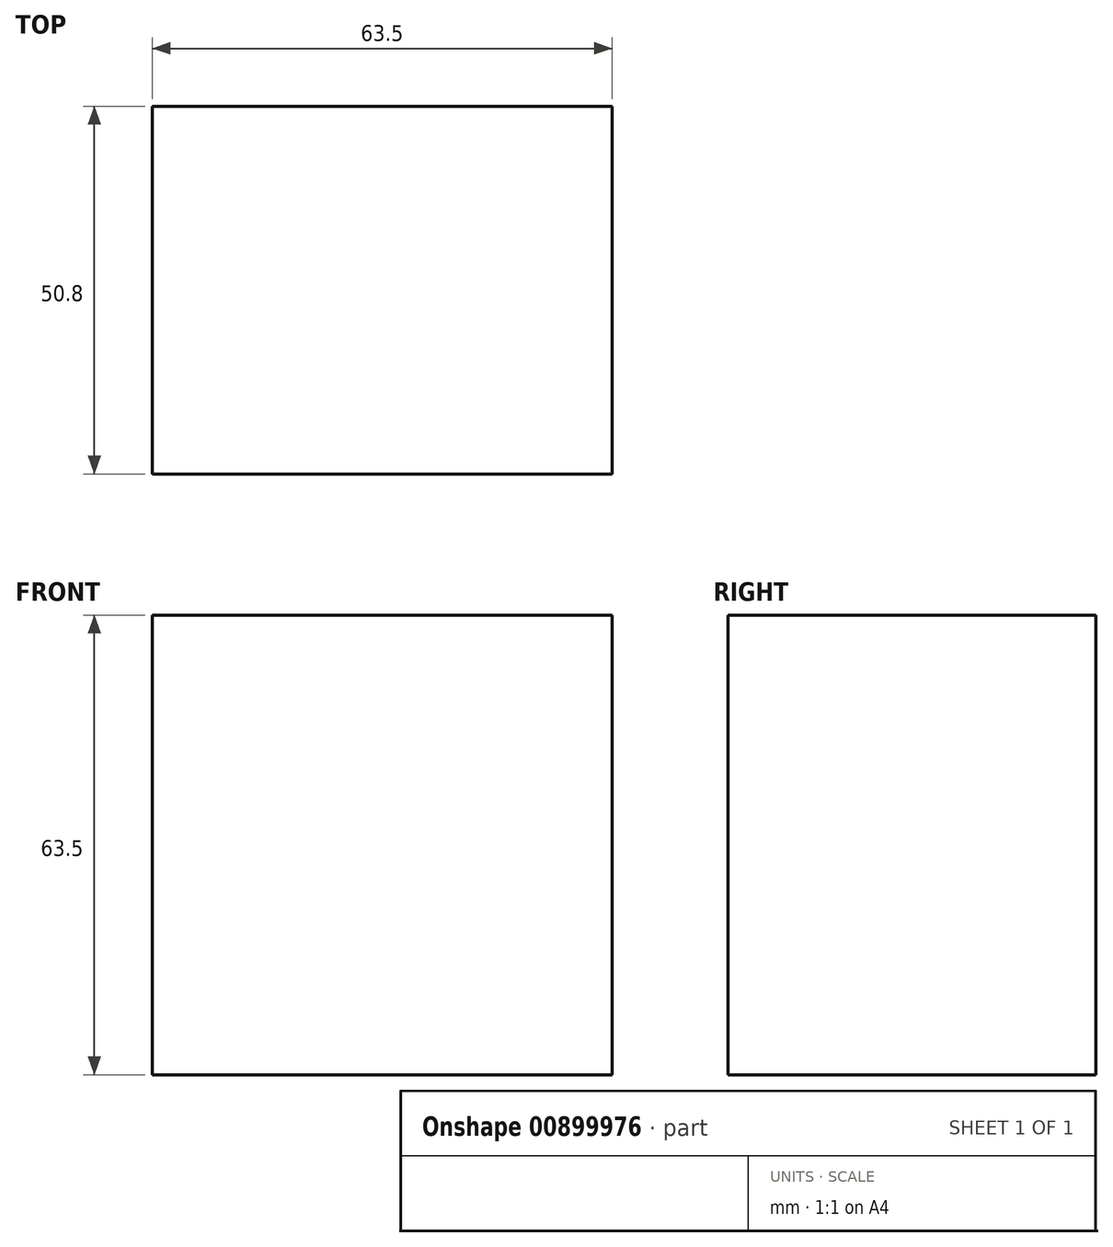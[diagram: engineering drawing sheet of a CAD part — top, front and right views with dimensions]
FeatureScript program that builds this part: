
annotation { "Feature Type Name" : "Feature", "Feature Type Description" : "" }
export const myFeature = defineFeature(function(context is Context, id is Id, definition is map)
    precondition{}
    {
        {
            var Q0;
            Q0=qCreatedBy(makeId("Front.planeOp"),FACE);
            var sketch = newSketch(context, id + "F0", { "sketchPlane" : qUnion([Q0])});
            skLineSegment(sketch, "E0", {"start": v(-33.27, 40.86) * mm, "end": v(30.23, 40.86) * mm});
            skLineSegment(sketch, "E1", {"start": v(30.23, 40.86) * mm, "end": v(30.23, -22.64) * mm});
            skLineSegment(sketch, "E2", {"start": v(30.23, -22.64) * mm, "end": v(-33.27, -22.64) * mm});
            skLineSegment(sketch, "E3", {"start": v(-33.27, -22.64) * mm, "end": v(-33.27, 40.86) * mm});
            skSolve(sketch);
        }
        {
            var Q0;
            Q0=makeQuery(id+"F0.imprint","IMPRINT",FACE,{"disambiguationData":[TD([[makeQuery(id+"F0.imprint","IMPRINT",EDGE,{"derivedFrom":sQuery(id+"F0.wireOp",EDGE,"E0")}),-1.0]])]});
            extrude(context, id + "F1", {"entities" : qUnion([Q0]), "depth" : 50.8 * mm, "offsetDistance" : 25.4 * mm});
        }
    });
